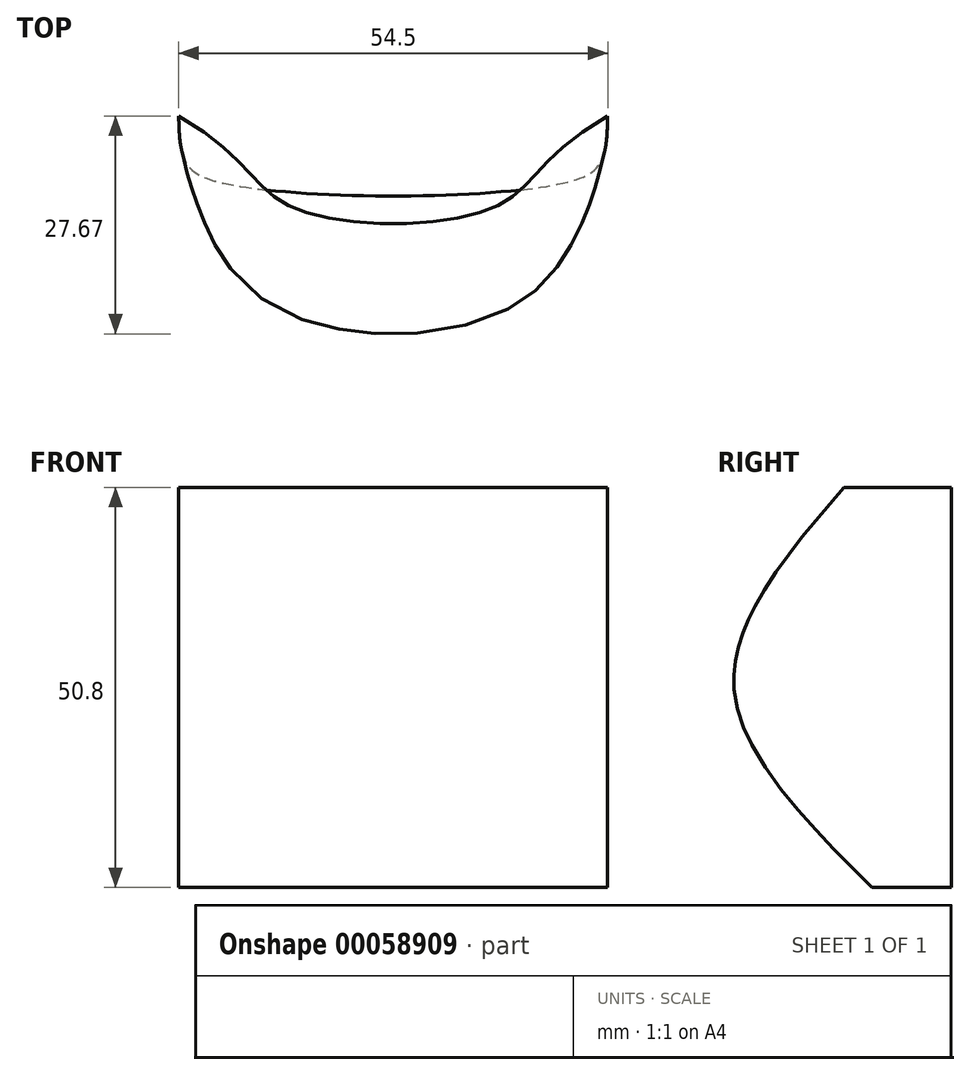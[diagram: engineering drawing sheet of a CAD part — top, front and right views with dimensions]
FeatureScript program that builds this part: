
annotation { "Feature Type Name" : "Feature", "Feature Type Description" : "" }
export const myFeature = defineFeature(function(context is Context, id is Id, definition is map)
    precondition{}
    {
        {
            var Q0;
            Q0=qCreatedBy(makeId("Front.planeOp"),FACE);
            var sketch = newSketch(context, id + "F0", { "sketchPlane" : qUnion([Q0])});
            skLineSegment(sketch, "E0.rect.bottom", {"start": v(27.25, -29.7) * mm, "end": v(-27.25, -29.7) * mm, "construction": true});
            skLineSegment(sketch, "E0.rect.top", {"start": v(27.25, 29.7) * mm, "end": v(-27.25, 29.7) * mm, "construction": true});
            skLineSegment(sketch, "E0.rect.left", {"start": v(27.25, -29.7) * mm, "end": v(27.25, 29.7) * mm, "construction": true});
            skLineSegment(sketch, "E0.rect.right", {"start": v(-27.25, -29.7) * mm, "end": v(-27.25, 29.7) * mm, "construction": true});
            skPoint(sketch, "E0.rect.middle", {"position": v(0, 0) * mm});
            skSolve(sketch);
        }
        {
            var Q0;
            Q0=qCreatedBy(makeId("Top.planeOp"),FACE);
            cPlane(context, id + "F1", {"entities" : qUnion([Q0]), "cplaneType" : CPlaneType.OFFSET, "offset" : 25.4 * mm, "width" : 152.4 * mm, "height" : 152.4 * mm});
        }
        {
            var Q0;
            Q0=qCreatedBy(makeId("Top.planeOp"),FACE);
            cPlane(context, id + "F2", {"entities" : qUnion([Q0]), "cplaneType" : CPlaneType.OFFSET, "offset" : 25.4 * mm, "oppositeDirection" : true, "width" : 152.4 * mm, "height" : 152.4 * mm});
        }
        {
            var Q0;
            Q0=qCreatedBy(id+"F1.planeOp",FACE);
            var sketch = newSketch(context, id + "F3", { "sketchPlane" : qUnion([Q0])});
            skFitSpline(sketch, "E1", {"points": [v(-27.25, 0) * mm, v(-12.8, -11.6) * mm, v(12.8, -11.6) * mm, v(27.25, 0) * mm], "startDerivative": vector(84.31, -46.73) * mm, "endDerivative": vector(84.31, 46.73) * mm});
            skLineSegment(sketch, "E2", {"start": v(0, 8.4) * mm, "end": v(0, -32.4) * mm, "construction": true});
            skSolve(sketch);
        }
        {
            var Q0;
            Q0=qCreatedBy(id+"F2.planeOp",FACE);
            var sketch = newSketch(context, id + "F4", { "sketchPlane" : qUnion([Q0])});
            skFitSpline(sketch, "E3", {"points": [v(-27.25, 0) * mm, v(-22.46, -8.3) * mm, v(22.46, -8.3) * mm, v(27.25, 0) * mm], "startDerivative": vector(1.6, -68.82) * mm, "endDerivative": vector(1.6, 68.82) * mm});
            skSolve(sketch);
        }
        {
            var Q0;
            Q0=qCreatedBy(makeId("Top.planeOp"),FACE);
            var sketch = newSketch(context, id + "F5", { "sketchPlane" : qUnion([Q0])});
            skFitSpline(sketch, "E4", {"points": [v(-27.25, 0) * mm, v(-16.84, -23.13) * mm, v(16.84, -23.13) * mm, v(27.25, 0) * mm], "startDerivative": vector(24.73, -77.16) * mm, "endDerivative": vector(24.73, 77.16) * mm});
            skSolve(sketch);
        }
        {
            var Q0;
            Q0=qCreatedBy(makeId("Right.planeOp"),FACE);
            cPlane(context, id + "F6", {"entities" : qUnion([Q0]), "cplaneType" : CPlaneType.OFFSET, "offset" : 12.7 * mm, "width" : 152.4 * mm, "height" : 152.4 * mm});
        }
        {
            var Q0;
            Q0=qCreatedBy(makeId("Top.planeOp"),FACE);
            cPlane(context, id + "F7", {"entities" : qUnion([Q0]), "cplaneType" : CPlaneType.OFFSET, "offset" : 12.7 * mm, "width" : 152.4 * mm, "height" : 152.4 * mm});
        }
        {
            var Q0;
            Q0=sQuery(id+"F4.wireOp",EDGE,"E3");
            var Q1;
            Q1=sQuery(id+"F5.wireOp",EDGE,"E4");
            var Q2;
            Q2=sQuery(id+"F3.wireOp",EDGE,"E1");
            loft(context, id + "F8", {"bodyType" : ToolBodyType.SURFACE, "wireProfilesArray" : [{ "wireProfileEntities" : qUnion([Q0]) }, { "wireProfileEntities" : qUnion([Q1]) }, { "wireProfileEntities" : qUnion([Q2]) }]});
        }
        {
            var Q0;
            Q0=qCreatedBy(id+"F7.planeOp",FACE);
            var sketch = newSketch(context, id + "F9", { "sketchPlane" : qUnion([Q0])});
            skFitSpline(sketch, "E5", {"points": [v(-27.25, 0) * mm, v(-25.12, -2.73) * mm, v(-23.76, -5.7) * mm, v(-21.89, -9.98) * mm, v(-21.3, -11.38) * mm, v(-20.31, -13.38) * mm, v(-19.97, -14.03) * mm, v(-19.24, -15.29) * mm, v(-18.86, -15.9) * mm, v(-17.59, -17.62) * mm, v(-16.6, -18.66) * mm, v(-14.16, -20.46) * mm, v(-12.7, -21.2) * mm, v(-7.82, -23) * mm, v(-3.9, -23.6) * mm, v(3.9, -23.6) * mm, v(7.82, -23) * mm, v(12.7, -21.2) * mm, v(14.16, -20.46) * mm, v(16.6, -18.66) * mm, v(17.59, -17.62) * mm, v(18.86, -15.9) * mm, v(19.24, -15.29) * mm, v(19.97, -14.03) * mm, v(20.31, -13.38) * mm, v(21.3, -11.38) * mm, v(21.89, -9.98) * mm, v(23.76, -5.7) * mm, v(25.12, -2.73) * mm, v(27.25, 0) * mm]});
            skLineSegment(sketch, "E6", {"start": v(12.71, -21.12) * mm, "end": v(16.64, -29.53) * mm});
            skSolve(sketch);
        }
        {
            var Q0;
            Q0=sQuery(id+"F9.wireOp",EDGE,"E5");
            var Q1;
            Q1=sQuery(id+"F9.wireOp",VERTEX,"E6.start");
            cPlane(context, id + "F10", {"entities" : qUnion([Q0, Q1]), "cplaneType" : CPlaneType.CURVE_POINT, "offset" : 152.4 * mm, "width" : 152.4 * mm, "height" : 152.4 * mm});
        }
        {
            var Q0;
            Q0=qCreatedBy(id+"F10.planeOp",FACE);
            var sketch = newSketch(context, id + "F11", { "sketchPlane" : qUnion([Q0])});
            skLineSegment(sketch, "E7", {"start": v(-28.96, 15.2) * mm, "end": v(-24.52, 12.7) * mm});
            skFitSpline(sketch, "E8", {"points": [v(-15.36, 25.4) * mm, v(-15.97, 24.66) * mm, v(-16.58, 23.91) * mm, v(-17.18, 23.16) * mm, v(-18.2, 21.9) * mm, v(-20.19, 19.35) * mm, v(-22.97, 15.38) * mm, v(-25.01, 11.92) * mm, v(-26.23, 9.36) * mm, v(-26.84, 7.85) * mm, v(-27.4, 6.33) * mm, v(-27.84, 4.77) * mm, v(-28.15, 3.19) * mm, v(-28.32, 1.97) * mm, v(-28.4, 0.76) * mm, v(-28.4, -0.85) * mm, v(-28.2, -2.44) * mm, v(-27.86, -4.02) * mm, v(-27.42, -5.59) * mm, v(-26.7, -7.48) * mm, v(-25.63, -9.64) * mm, v(-24.8, -11.02) * mm, v(-24.37, -11.7) * mm, v(-23.95, -12.35) * mm, v(-23.08, -13.62) * mm, v(-21.22, -16.05) * mm, v(-18.72, -18.93) * mm, v(-15.53, -22.22) * mm, v(-13.33, -24.34) * mm, v(-12.23, -25.4) * mm]});
            skSolve(sketch);
        }
    });
